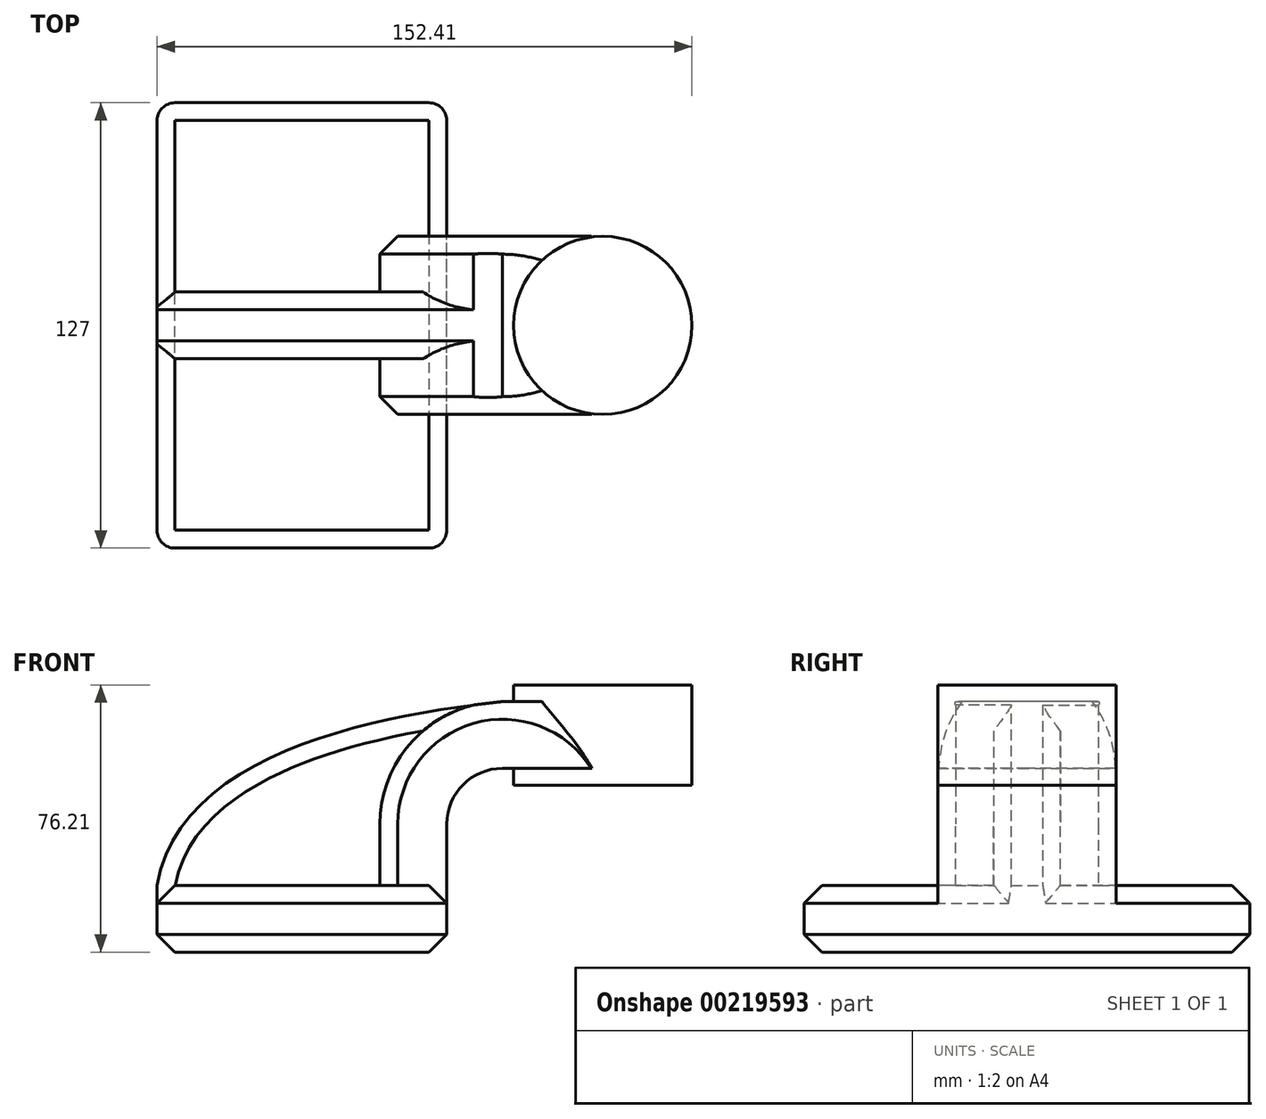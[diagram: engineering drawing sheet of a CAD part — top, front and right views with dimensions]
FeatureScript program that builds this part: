
annotation { "Feature Type Name" : "Feature", "Feature Type Description" : "" }
export const myFeature = defineFeature(function(context is Context, id is Id, definition is map)
    precondition{}
    {
        {
            var Q0;
            Q0=qCreatedBy(makeId("Front.planeOp"),FACE);
            var sketch = newSketch(context, id + "F0", { "sketchPlane" : qUnion([Q0])});
            skLineSegment(sketch, "E0.bottom", {"start": v(41.28, 9.53) * mm, "end": v(-41.28, 9.53) * mm});
            skLineSegment(sketch, "E0.top", {"start": v(41.28, -9.52) * mm, "end": v(-41.28, -9.52) * mm});
            skLineSegment(sketch, "E0.left", {"start": v(41.28, 9.53) * mm, "end": v(41.28, -9.52) * mm});
            skLineSegment(sketch, "E0.right", {"start": v(-41.28, 9.53) * mm, "end": v(-41.28, -9.52) * mm});
            skPoint(sketch, "E0.middle", {"position": v(0, 0) * mm});
            skLineSegment(sketch, "E1.bottom", {"start": v(111.12, 66.68) * mm, "end": v(60.32, 66.68) * mm});
            skLineSegment(sketch, "E1.top", {"start": v(111.12, 38.1) * mm, "end": v(60.32, 38.1) * mm});
            skLineSegment(sketch, "E1.left", {"start": v(111.12, 66.68) * mm, "end": v(111.12, 38.1) * mm});
            skLineSegment(sketch, "E1.right", {"start": v(60.32, 66.68) * mm, "end": v(60.32, 38.1) * mm});
            skPoint(sketch, "E1.middle", {"position": v(85.72, 52.39) * mm});
            skLineSegment(sketch, "E2", {"start": v(41.28, 9.53) * mm, "end": v(41.28, 27) * mm});
            skArc(sketch, "E3", {"start": v(41.27, 27) * mm, "mid": v(45.92, 38.23) * mm, "end": v(57.15, 42.88) * mm});
            skLineSegment(sketch, "E4", {"start": v(57.15, 42.88) * mm, "end": v(85.72, 42.88) * mm});
            skLineSegment(sketch, "E5.0", {"start": v(57.15, 61.93) * mm, "end": v(85.72, 61.93) * mm});
            skArc(sketch, "E5.1", {"start": v(22.22, 27) * mm, "mid": v(32.45, 51.7) * mm, "end": v(57.15, 61.93) * mm});
            skLineSegment(sketch, "E5.2", {"start": v(22.23, 9.53) * mm, "end": v(22.23, 27) * mm});
            skLineSegment(sketch, "E6", {"start": v(85.72, 38.1) * mm, "end": v(85.72, 66.68) * mm});
            skFitSpline(sketch, "E7", {"points": [v(-41.28, 9.53) * mm, v(57.15, 61.93) * mm], "startDerivative": vector(19.35, 115.01) * mm, "endDerivative": vector(103.38, 11.4) * mm});
            skSolve(sketch);
        }
        {
            var Q0;
            Q0=makeQuery(id+"F0.imprint","IMPRINT",FACE,{"disambiguationData":[TD([[makeQuery(id+"F0.imprint","IMPRINT",EDGE,{"derivedFrom":sQuery(id+"F0.wireOp",EDGE,"E0.top")}),-1.0]])]});
            extrude(context, id + "F1", {"entities" : qUnion([Q0]), "endBound" : BoundingType.SYMMETRIC, "depth" : 127 * mm});
        }
        {
            var Q0;
            {var subQ1=sQuery(id+"F0.wireOp",EDGE,"E2");Q0=makeQuery(id+"F0.imprint","IMPRINT",FACE,{"disambiguationData":[TD([[makeQuery(id+"F0.imprint","IMPRINT",EDGE,{"derivedFrom":subQ1}),1.0]])]});}
            var Q1;
            {var subQ0=sQuery(id+"F0.wireOp",EDGE,"E5.0");var subQ1=sQuery(id+"F0.wireOp",EDGE,"E1.right");var subQ2=makeQuery(id+"F0.imprint","INTERSECT",VERTEX,{"derivedFrom":[subQ1,subQ0]});Q1=makeQuery(id+"F0.imprint","IMPRINT",FACE,{"disambiguationData":[TD([[makeQuery(id+"F0.imprint","IMPRINT",EDGE,{"disambiguationData":[TD([[subQ2,-1.0]])],"derivedFrom":subQ1}),1.0]])]});}
            extrude(context, id + "F2", {"entities" : qUnion([Q0, Q1]), "operationType" : NewBodyOperationType.ADD, "endBound" : BoundingType.SYMMETRIC, "depth" : 50.8 * mm});
        }
        {
            var Q0;
            {var subQ3=sQuery(id+"F0.wireOp",EDGE,"E5.2");Q0=makeQuery(id+"F0.imprint","IMPRINT",FACE,{"disambiguationData":[TD([[makeQuery(id+"F0.imprint","IMPRINT",EDGE,{"derivedFrom":subQ3}),1.0]])]});}
            extrude(context, id + "F3", {"entities" : qUnion([Q0]), "operationType" : NewBodyOperationType.ADD, "endBound" : BoundingType.SYMMETRIC, "depth" : 19.05 * mm});
        }
        {
            var Q0;
            {var subQ0=sQuery(id+"F0.wireOp",EDGE,"E1.left");Q0=makeQuery(id+"F0.imprint","IMPRINT",FACE,{"disambiguationData":[TD([[makeQuery(id+"F0.imprint","IMPRINT",EDGE,{"derivedFrom":subQ0}),-1.0]])]});}
            var Q1;
            Q1=sQuery(id+"F0.wireOp",EDGE,"E6");
            revolve(context, id + "F4", {"operationType" : NewBodyOperationType.ADD, "entities" : qUnion([Q0]), "axis" : qUnion([Q1]), "revolveType" : RevolveType.FULL});
        }
        {
            var Q0;
            Q0=makeQuery(id+"F1.opExtrude","CAP_EDGE",EDGE,{"disambiguationData":[OSD([sQuery(id+"F0.wireOp",EDGE,"E0.left")])],"isStart":false});
            var Q1;
            Q1=makeQuery(id+"F1.opExtrude","CAP_EDGE",EDGE,{"disambiguationData":[OSD([sQuery(id+"F0.wireOp",EDGE,"E0.left")])],"isStart":true});
            var Q2;
            Q2=makeQuery(id+"F1.opExtrude","CAP_EDGE",EDGE,{"disambiguationData":[OSD([sQuery(id+"F0.wireOp",EDGE,"E0.right")])],"isStart":true});
            var Q3;
            Q3=makeQuery(id+"F1.opExtrude","CAP_EDGE",EDGE,{"disambiguationData":[OSD([sQuery(id+"F0.wireOp",EDGE,"E0.right")])],"isStart":false});
            fillet(context, id + "F5", {"entities" : qUnion([Q0, Q1, Q2, Q3]), "radius" : 5.08 * mm, "tangentPropagation" : true, "allowEdgeOverflow" : false});
        }
        {
            var Q0;
            Q0=makeQuery(id+"F1.opExtrude","SWEPT_EDGE",EDGE,{"disambiguationData":[OSD([sQuery(id+"F0.wireOp",EDGE,"E0.top"),sQuery(id+"F0.wireOp",EDGE,"E0.right")])]});
            var Q1;
            Q1=makeQuery(id+"F1.opExtrude","CAP_EDGE",EDGE,{"disambiguationData":[OSD([sQuery(id+"F0.wireOp",EDGE,"E0.bottom")])],"isStart":true});
            var Q2;
            Q2=makeQuery(id+"F1.opExtrude","CAP_EDGE",EDGE,{"disambiguationData":[OSD([sQuery(id+"F0.wireOp",EDGE,"E0.bottom")])],"isStart":false});
            chamfer(context, id + "F6", {"entities" : qUnion([Q0, Q1, Q2]), "width" : 5.08 * mm, "tangentPropagation" : true});
        }
        {
            var Q0;
            Q0=makeQuery(id+"F3.opExtrude","CAP_EDGE",EDGE,{"disambiguationData":[OSD([sQuery(id+"F0.wireOp",EDGE,"E7")])],"isStart":false});
            var Q1;
            Q1=makeQuery(id+"F3.opExtrude","CAP_EDGE",EDGE,{"disambiguationData":[OSD([sQuery(id+"F0.wireOp",EDGE,"E7")])],"isStart":true});
            var Q2;
            Q2=makeQuery(id+"F2.opExtrude","CAP_EDGE",EDGE,{"disambiguationData":[OSD([sQuery(id+"F0.wireOp",EDGE,"E5.1")])],"isStart":true});
            var Q3;
            Q3=makeQuery(id+"F2.opExtrude","CAP_EDGE",EDGE,{"disambiguationData":[OSD([sQuery(id+"F0.wireOp",EDGE,"E5.1")])],"isStart":false});
            chamfer(context, id + "F7", {"entities" : qUnion([Q0, Q1, Q2, Q3]), "width" : 5.08 * mm, "tangentPropagation" : true});
        }
    });
